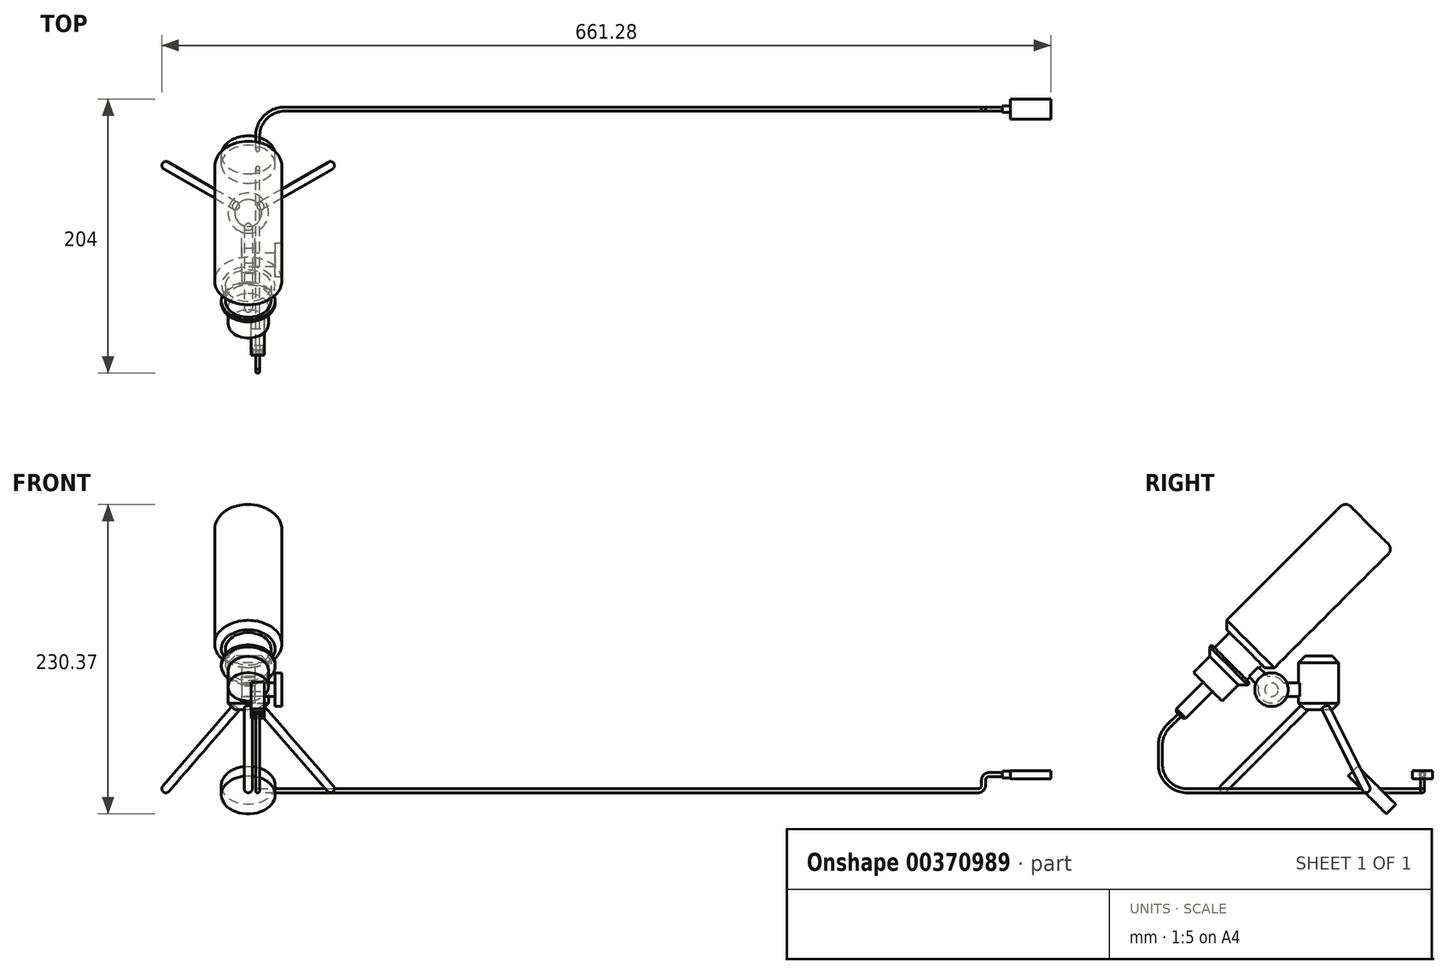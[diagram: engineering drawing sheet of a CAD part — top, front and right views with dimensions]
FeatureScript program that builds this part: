
annotation { "Feature Type Name" : "Feature", "Feature Type Description" : "" }
export const myFeature = defineFeature(function(context is Context, id is Id, definition is map)
    precondition{}
    {
        {
            var Q0;
            Q0=qCreatedBy(makeId("Top.planeOp"),FACE);
            var sketch = newSketch(context, id + "F0", { "sketchPlane" : qUnion([Q0])});
            skCircle(sketch, "E0", {"center": v(0, 0) * mm, "radius": 15 * mm});
            skSolve(sketch);
        }
        {
            var Q0;
            Q0=qSketchRegion(id+"F0",true);
            extrude(context, id + "F1", {"entities" : qUnion([Q0]), "depth" : 40 * mm});
        }
        {
            var Q0;
            Q0=makeQuery(id+"F1.opExtrude","CAP_EDGE",EDGE,{"disambiguationData":[OSD([sQuery(id+"F0.wireOp",EDGE,"E0")])],"isStart":true});
            var Q1;
            Q1=makeQuery(id+"F1.opExtrude","CAP_EDGE",EDGE,{"disambiguationData":[OSD([sQuery(id+"F0.wireOp",EDGE,"E0")])],"isStart":false});
            chamfer(context, id + "F2", {"entities" : qUnion([Q0, Q1]), "width" : 5 * mm, "tangentPropagation" : true});
        }
        {
            var Q0;
            Q0=qCreatedBy(makeId("Right.planeOp"),FACE);
            var sketch = newSketch(context, id + "F3", { "sketchPlane" : qUnion([Q0])});
            skLineSegment(sketch, "E1", {"start": v(-72.83, -56.59) * mm, "end": v(-2.12, 14.12) * mm});
            skLineSegment(sketch, "E2", {"start": v(-2.12, 14.12) * mm, "end": v(0, 12) * mm});
            skArc(sketch, "E3", {"start": v(-72.83, -56.59) * mm, "mid": v(-73.71, -58.71) * mm, "end": v(-72.83, -60.83) * mm});
            skLineSegment(sketch, "E4", {"start": v(-72.83, -60.83) * mm, "end": v(0, 12) * mm});
            skSolve(sketch);
        }
        {
            var Q0;
            Q0=qSketchRegion(id+"F3",true);
            var Q1;
            Q1=sQuery(id+"F3.wireOp",EDGE,"E4");
            revolve(context, id + "F4", {"operationType" : NewBodyOperationType.ADD, "entities" : qUnion([Q0]), "axis" : qUnion([Q1]), "revolveType" : RevolveType.FULL});
        }
        {
            var Q0;
            Q0=qCreatedBy(makeId("Right.planeOp"),FACE);
            var sketch = newSketch(context, id + "F5", { "sketchPlane" : qUnion([Q0])});
            skLineSegment(sketch, "E5", {"start": v(0, 0) * mm, "end": v(0, -28.47) * mm});
            skSolve(sketch);
        }
        {
            var Q0;
            Q0=qCreatedBy(makeId("Right.planeOp"),FACE);
            var Q1;
            Q1=sQuery(id+"F5.wireOp",EDGE,"E5");
            cPlane(context, id + "F6", {"entities" : qUnion([Q0, Q1]), "cplaneType" : CPlaneType.LINE_ANGLE, "offset" : 25 * mm, "angle" : 120 * degree, "oppositeDirection" : true, "width" : 150 * mm, "height" : 150 * mm});
        }
        {
            var Q0;
            Q0=qCreatedBy(id+"F6.planeOp",FACE);
            var sketch = newSketch(context, id + "F7", { "sketchPlane" : qUnion([Q0])});
            skLineSegment(sketch, "E6", {"start": v(0, 12) * mm, "end": v(72.73, -60.73) * mm});
            skLineSegment(sketch, "E7", {"start": v(72.73, -56.5) * mm, "end": v(2.02, 14.22) * mm});
            skLineSegment(sketch, "E8", {"start": v(2.02, 14.22) * mm, "end": v(0, 12) * mm});
            skArc(sketch, "E9", {"start": v(72.73, -56.5) * mm, "mid": v(73.61, -58.61) * mm, "end": v(72.73, -60.73) * mm});
            skPoint(sketch, "E10.orphan", {"position": v(70.61, -61.61) * mm});
            skSolve(sketch);
        }
        {
            var Q0;
            Q0=qSketchRegion(id+"F7",true);
            var Q1;
            Q1=sQuery(id+"F7.wireOp",EDGE,"E6");
            revolve(context, id + "F8", {"operationType" : NewBodyOperationType.ADD, "entities" : qUnion([Q0]), "axis" : qUnion([Q1]), "revolveType" : RevolveType.FULL});
        }
        {
            var Q0;
            Q0=qCreatedBy(id+"F6.planeOp",FACE);
            var Q1;
            Q1=sQuery(id+"F5.wireOp",EDGE,"E5");
            cPlane(context, id + "F9", {"entities" : qUnion([Q0, Q1]), "cplaneType" : CPlaneType.LINE_ANGLE, "offset" : 25 * mm, "angle" : 120 * degree, "oppositeDirection" : true, "width" : 150 * mm, "height" : 150 * mm});
        }
        {
            var Q0;
            Q0=qCreatedBy(id+"F9.planeOp",FACE);
            var sketch = newSketch(context, id + "F10", { "sketchPlane" : qUnion([Q0])});
            skLineSegment(sketch, "E11", {"start": v(0, 12) * mm, "end": v(-72.89, -60.89) * mm});
            skLineSegment(sketch, "E12", {"start": v(-72.89, -56.64) * mm, "end": v(-2.18, 14.07) * mm});
            skLineSegment(sketch, "E13", {"start": v(-2.18, 14.07) * mm, "end": v(0, 12) * mm});
            skArc(sketch, "E14", {"start": v(-72.89, -56.64) * mm, "mid": v(-73.77, -58.77) * mm, "end": v(-72.89, -60.89) * mm});
            skPoint(sketch, "E15.orphan", {"position": v(-70.77, -61.77) * mm});
            skSolve(sketch);
        }
        {
            var Q0;
            Q0=qSketchRegion(id+"F10",true);
            var Q1;
            Q1=sQuery(id+"F10.wireOp",EDGE,"E11");
            revolve(context, id + "F11", {"operationType" : NewBodyOperationType.ADD, "entities" : qUnion([Q0]), "axis" : qUnion([Q1]), "revolveType" : RevolveType.FULL});
        }
        {
            var Q0;
            Q0=qCreatedBy(makeId("Front.planeOp"),FACE);
            var sketch = newSketch(context, id + "F12", { "sketchPlane" : qUnion([Q0])});
            skLineSegment(sketch, "E16.bottom", {"start": v(-5, 20) * mm, "end": v(5, 20) * mm});
            skLineSegment(sketch, "E16.top", {"start": v(-5, 10) * mm, "end": v(5, 10) * mm});
            skLineSegment(sketch, "E16.left", {"start": v(-5, 20) * mm, "end": v(-5, 10) * mm});
            skLineSegment(sketch, "E16.right", {"start": v(5, 20) * mm, "end": v(5, 10) * mm});
            skSolve(sketch);
        }
        {
            var Q0;
            Q0=qSketchRegion(id+"F12",true);
            extrude(context, id + "F13", {"entities" : qUnion([Q0]), "operationType" : NewBodyOperationType.ADD, "depth" : 30 * mm});
        }
        {
            var Q0;
            Q0=qCreatedBy(makeId("Right.planeOp"),FACE);
            var sketch = newSketch(context, id + "F14", { "sketchPlane" : qUnion([Q0])});
            skCircle(sketch, "E17", {"center": v(-35, 15) * mm, "radius": 10 * mm});
            skLineSegment(sketch, "E18", {"start": v(-38.54, 11.46) * mm, "end": v(-35, 15) * mm});
            skLineSegment(sketch, "E19", {"start": v(-38.54, 11.46) * mm, "end": v(-52.68, 25.6) * mm});
            skLineSegment(sketch, "E20", {"start": v(-52.68, 25.6) * mm, "end": v(-45.6, 32.68) * mm});
            skLineSegment(sketch, "E21", {"start": v(-45.6, 32.68) * mm, "end": v(-31.46, 18.54) * mm});
            skLineSegment(sketch, "E22", {"start": v(-31.46, 18.54) * mm, "end": v(-35, 15) * mm});
            skSolve(sketch);
        }
        {
            var Q0;
            Q0=qSketchRegion(id+"F14",true);
            extrude(context, id + "F15", {"entities" : qUnion([Q0]), "operationType" : NewBodyOperationType.ADD, "endBound" : BoundingType.SYMMETRIC, "depth" : 10 * mm});
        }
        {
            var Q0;
            Q0=makeQuery(id+"F15.opExtrude","SWEPT_FACE",FACE,{"disambiguationData":[OSD([sQuery(id+"F14.wireOp",EDGE,"E21")])]});
            var sketch = newSketch(context, id + "F16", { "sketchPlane" : qUnion([Q0])});
            skPoint(sketch, "E23.first.point", {"position": v(0, -67.78) * mm});
            skPoint(sketch, "E23.first.point.positionSnap0", {"position": v(0, -55.36) * mm});
            skPoint(sketch, "E23.second.point", {"position": v(0, -49.63) * mm});
            skPoint(sketch, "E23.second.point.positionSnap0", {"position": v(0, -55.36) * mm});
            skPoint(sketch, "E23.third.point", {"position": v(-9.57, -55.36) * mm});
            skPoint(sketch, "E23.third.point.positionSnap0", {"position": v(0, -55.36) * mm});
            skCircle(sketch, "E24", {"center": v(0, -70.36) * mm, "radius": 20 * mm});
            skSolve(sketch);
        }
        {
            var Q0;
            Q0=qSketchRegion(id+"F16",true);
            extrude(context, id + "F17", {"entities" : qUnion([Q0]), "operationType" : NewBodyOperationType.ADD, "oppositeDirection" : true, "depth" : 10 * mm});
        }
        {
            var Q0;
            Q0=qCreatedBy(makeId("Right.planeOp"),FACE);
            var sketch = newSketch(context, id + "F18", { "sketchPlane" : qUnion([Q0])});
            skLineSegment(sketch, "E25", {"start": v(-82.38, 17.12) * mm, "end": v(37.83, 137.33) * mm});
            skLineSegment(sketch, "E26", {"start": v(37.83, 137.33) * mm, "end": v(20.15, 155) * mm});
            skLineSegment(sketch, "E27", {"start": v(20.15, 155) * mm, "end": v(-71.77, 63.08) * mm});
            skLineSegment(sketch, "E28", {"start": v(-71.77, 63.08) * mm, "end": v(-66.11, 57.43) * mm});
            skLineSegment(sketch, "E29", {"start": v(-66.11, 57.43) * mm, "end": v(-77.43, 46.11) * mm});
            skLineSegment(sketch, "E30", {"start": v(-84.5, 43.28) * mm, "end": v(-80.96, 39.75) * mm});
            skLineSegment(sketch, "E31", {"start": v(-89.45, 24.2) * mm, "end": v(-82.38, 17.12) * mm});
            skPoint(sketch, "E32.end.orphan", {"position": v(-71.77, 45.43) * mm});
            skLineSegment(sketch, "E33", {"start": v(-77.43, 46.11) * mm, "end": v(-79.55, 48.23) * mm});
            skLineSegment(sketch, "E34", {"start": v(-79.55, 48.23) * mm, "end": v(-84.5, 43.28) * mm});
            skLineSegment(sketch, "E35", {"start": v(-80.96, 39.75) * mm, "end": v(-92.98, 27.73) * mm});
            skLineSegment(sketch, "E36", {"start": v(-92.98, 27.73) * mm, "end": v(-89.45, 24.2) * mm});
            skPoint(sketch, "E37.start.orphan", {"position": v(-77.43, 36.21) * mm});
            skSolve(sketch);
        }
        {
            var Q0;
            Q0=qSketchRegion(id+"F18",true);
            var Q1;
            Q1=sQuery(id+"F18.wireOp",EDGE,"E25");
            revolve(context, id + "F19", {"operationType" : NewBodyOperationType.ADD, "entities" : qUnion([Q0]), "axis" : qUnion([Q1]), "revolveType" : RevolveType.FULL});
        }
        {
            var Q0;
            Q0=makeQuery(id+"F19.opRevolve","SWEPT_EDGE",EDGE,{"disambiguationData":[OSD([sQuery(id+"F18.wireOp",EDGE,"E26"),sQuery(id+"F18.wireOp",EDGE,"E27")])]});
            fillet(context, id + "F20", {"entities" : qUnion([Q0]), "radius" : 5 * mm, "tangentPropagation" : true, "allowEdgeOverflow" : false});
        }
        {
            var Q0;
            Q0=makeQuery(id+"F19.opRevolve","SWEPT_EDGE",EDGE,{"disambiguationData":[OSD([sQuery(id+"F18.wireOp",EDGE,"E27"),sQuery(id+"F18.wireOp",EDGE,"E28")])]});
            var Q1;
            Q1=makeQuery(id+"F19.opRevolve","SWEPT_EDGE",EDGE,{"disambiguationData":[OSD([sQuery(id+"F18.wireOp",EDGE,"E30"),sQuery(id+"F18.wireOp",EDGE,"E34")])]});
            chamfer(context, id + "F21", {"entities" : qUnion([Q0, Q1]), "width" : 5 * mm, "tangentPropagation" : true});
        }
        {
            var Q0;
            Q0=makeQuery(id+"F15.boolean.opBoolean","MERGE",FACE,{"derivedFrom":[makeQuery(id+"F13.opExtrude","SWEPT_FACE",FACE,{"disambiguationData":[OSD([sQuery(id+"F12.wireOp",EDGE,"E16.right")])]}),makeQuery(id+"F15.opExtrude","CAP_FACE",FACE,{"disambiguationData":[OSD([sQuery(id+"F14.wireOp",EDGE,"E17"),sQuery(id+"F14.wireOp",EDGE,"E19"),sQuery(id+"F14.wireOp",EDGE,"E20"),sQuery(id+"F14.wireOp",EDGE,"E21")])],"isStart":false})]});
            var sketch = newSketch(context, id + "F22", { "sketchPlane" : qUnion([Q0])});
            skCircle(sketch, "E38", {"center": v(-35, 15) * mm, "radius": 5 * mm});
            skSolve(sketch);
        }
        {
            var Q0;
            Q0=qSketchRegion(id+"F22",true);
            extrude(context, id + "F23", {"entities" : qUnion([Q0]), "operationType" : NewBodyOperationType.ADD, "depth" : 15 * mm});
        }
        {
            var Q0;
            Q0=makeQuery(id+"F23.opExtrude","CAP_FACE",FACE,{"disambiguationData":[OSD([sQuery(id+"F22.wireOp",EDGE,"E38")])],"isStart":false});
            var sketch = newSketch(context, id + "F24", { "sketchPlane" : qUnion([Q0])});
            skCircle(sketch, "E39", {"center": v(-35, 15) * mm, "radius": 12.5 * mm});
            skSolve(sketch);
        }
        {
            var Q0;
            Q0=qSketchRegion(id+"F24",true);
            extrude(context, id + "F25", {"entities" : qUnion([Q0]), "operationType" : NewBodyOperationType.ADD, "depth" : 5 * mm});
        }
        {
            var Q0;
            Q0=makeQuery(id+"F19.opRevolve","SWEPT_FACE",FACE,{"disambiguationData":[OSD([sQuery(id+"F18.wireOp",EDGE,"E31")])]});
            var sketch = newSketch(context, id + "F26", { "sketchPlane" : qUnion([Q0])});
            skLineSegment(sketch, "E40.bottom", {"start": v(2, 65.36) * mm, "end": v(12, 65.36) * mm});
            skLineSegment(sketch, "E40.top", {"start": v(2, 75.36) * mm, "end": v(12, 75.36) * mm});
            skLineSegment(sketch, "E40.left", {"start": v(2, 65.36) * mm, "end": v(2, 75.36) * mm});
            skLineSegment(sketch, "E40.right", {"start": v(12, 65.36) * mm, "end": v(12, 75.36) * mm});
            skSolve(sketch);
        }
        {
            var Q0;
            Q0=qSketchRegion(id+"F26",true);
            extrude(context, id + "F27", {"entities" : qUnion([Q0]), "operationType" : NewBodyOperationType.ADD, "depth" : 30 * mm});
        }
        {
            var Q0;
            Q0=makeQuery(id+"F27.opExtrude","CAP_FACE",FACE,{"disambiguationData":[OSD([sQuery(id+"F26.wireOp",EDGE,"E40.bottom"),sQuery(id+"F26.wireOp",EDGE,"E40.top"),sQuery(id+"F26.wireOp",EDGE,"E40.left"),sQuery(id+"F26.wireOp",EDGE,"E40.right")])],"isStart":false});
            chamfer(context, id + "F28", {"entities" : qUnion([Q0]), "width" : 2 * mm, "tangentPropagation" : true});
        }
        {
            var Q0;
            Q0=qCreatedBy(makeId("Right.planeOp"),FACE);
            var sketch = newSketch(context, id + "F29", { "sketchPlane" : qUnion([Q0])});
            skLineSegment(sketch, "E41", {"start": v(-103.59, -4.1) * mm, "end": v(-111.87, -12.38) * mm});
            skLineSegment(sketch, "E42", {"start": v(-117.73, -26.52) * mm, "end": v(-117.73, -40.23) * mm});
            skLineSegment(sketch, "E43", {"start": v(-97.73, -60.23) * mm, "end": v(52.27, -60.23) * mm});
            skPoint(sketch, "E44.visualSharp", {"position": v(-117.73, -18.23) * mm});
            skArc(sketch, "E44.filletArc", {"start": v(-111.87, -12.38) * mm, "mid": v(-116.2, -18.86) * mm, "end": v(-117.73, -26.52) * mm});
            skPoint(sketch, "E45.visualSharp", {"position": v(-117.73, -60.23) * mm});
            skArc(sketch, "E45.filletArc", {"start": v(-117.73, -40.23) * mm, "mid": v(-111.87, -54.38) * mm, "end": v(-97.73, -60.23) * mm});
            skSolve(sketch);
        }
        {
            var Q0;
            Q0=makeQuery(id+"F27.opExtrude","CAP_FACE",FACE,{"disambiguationData":[OSD([sQuery(id+"F26.wireOp",EDGE,"E40.bottom"),sQuery(id+"F26.wireOp",EDGE,"E40.top"),sQuery(id+"F26.wireOp",EDGE,"E40.left"),sQuery(id+"F26.wireOp",EDGE,"E40.right")])],"isStart":false});
            var sketch = newSketch(context, id + "F30", { "sketchPlane" : qUnion([Q0])});
            skCircle(sketch, "E46", {"center": v(7, 70.36) * mm, "radius": 1.5 * mm});
            skSolve(sketch);
        }
        {
            var Q0;
            Q0=qSketchRegion(id+"F30",true);
            var Q1;
            Q1=qConstructionFilter(qBodyType(qCreatedBy(id+"F29",EDGE),BodyType.WIRE),ConstructionObject.NO);
            sweep(context, id + "F31", {"operationType" : NewBodyOperationType.ADD, "profiles" : qUnion([Q0]), "path" : qUnion([Q1])});
        }
        {
            var Q0;
            Q0=makeQuery(id+"F31.opSweep","CAP_FACE",FACE,{"disambiguationData":[OSD([sQuery(id+"F29.wireOp",VERTEX,"E43.end"),sQuery(id+"F30.wireOp",EDGE,"E46")])],"isStart":false});
            var sketch = newSketch(context, id + "F32", { "sketchPlane" : qUnion([Q0])});
            skCircle(sketch, "E47", {"center": v(-7, -60.23) * mm, "radius": 1.5 * mm});
            skSolve(sketch);
        }
        {
            var Q0;
            Q0=qBodyType(qCreatedBy(id+"F32",EDGE),BodyType.WIRE);
            cPlane(context, id + "F33", {"entities" : qUnion([Q0]), "cplaneType" : CPlaneType.LINE_ANGLE, "offset" : 25 * mm, "angle" : 0 * degree, "width" : 150 * mm, "height" : 150 * mm});
        }
        {
            var Q0;
            Q0=qCreatedBy(id+"F33.planeOp",FACE);
            var sketch = newSketch(context, id + "F34", { "sketchPlane" : qUnion([Q0])});
            skLineSegment(sketch, "E48", {"start": v(27, 77.27) * mm, "end": v(527, 77.27) * mm});
            skLineSegment(sketch, "E49", {"start": v(7, 52.27) * mm, "end": v(7, 57.27) * mm});
            skArc(sketch, "E50", {"start": v(7, 57.27) * mm, "mid": v(12.86, 71.41) * mm, "end": v(27, 77.27) * mm});
            skSolve(sketch);
        }
        {
            var Q0;
            Q0=qSketchRegion(id+"F32",true);
            var Q1;
            Q1=qConstructionFilter(qBodyType(qCreatedBy(id+"F34",EDGE),BodyType.WIRE),ConstructionObject.NO);
            sweep(context, id + "F35", {"operationType" : NewBodyOperationType.ADD, "profiles" : qUnion([Q0]), "path" : qUnion([Q1])});
        }
        {
            var Q0;
            Q0=makeQuery(id+"F35.opSweep","CAP_FACE",FACE,{"disambiguationData":[OSD([sQuery(id+"F32.wireOp",EDGE,"E47"),sQuery(id+"F34.wireOp",VERTEX,"E48.end")])],"isStart":false});
            var sketch = newSketch(context, id + "F36", { "sketchPlane" : qUnion([Q0])});
            skCircle(sketch, "E51", {"center": v(77.27, -60.23) * mm, "radius": 1.5 * mm});
            skSolve(sketch);
        }
        {
            var Q0;
            Q0=sQuery(id+"F36.wireOp",EDGE,"E51");
            cPlane(context, id + "F37", {"entities" : qUnion([Q0]), "cplaneType" : CPlaneType.LINE_ANGLE, "offset" : 25 * mm, "angle" : 0 * degree, "width" : 150 * mm, "height" : 150 * mm});
        }
        {
            var Q0;
            Q0=qCreatedBy(id+"F37.planeOp",FACE);
            var sketch = newSketch(context, id + "F38", { "sketchPlane" : qUnion([Q0])});
            skLineSegment(sketch, "E52", {"start": v(-527, -60.23) * mm, "end": v(-543, -60.23) * mm});
            skLineSegment(sketch, "E53", {"start": v(-547, -56.23) * mm, "end": v(-547, -52.23) * mm});
            skLineSegment(sketch, "E54", {"start": v(-551, -48.23) * mm, "end": v(-567, -48.23) * mm});
            skArc(sketch, "E55", {"start": v(-543, -60.23) * mm, "mid": v(-545.83, -59.06) * mm, "end": v(-547, -56.23) * mm});
            skArc(sketch, "E56", {"start": v(-547, -52.23) * mm, "mid": v(-548.17, -49.4) * mm, "end": v(-551, -48.23) * mm});
            skPoint(sketch, "E57.0", {"position": v(-527, -60.23) * mm});
            skSolve(sketch);
        }
        {
            var Q0;
            Q0=qSketchRegion(id+"F36",true);
            var Q1;
            Q1=qConstructionFilter(qBodyType(qCreatedBy(id+"F38",EDGE),BodyType.WIRE),ConstructionObject.NO);
            sweep(context, id + "F39", {"operationType" : NewBodyOperationType.ADD, "profiles" : qUnion([Q0]), "path" : qUnion([Q1])});
        }
        {
            var Q0;
            Q0=makeQuery(id+"F39.opSweep","CAP_FACE",FACE,{"disambiguationData":[OSD([sQuery(id+"F36.wireOp",EDGE,"E51"),sQuery(id+"F38.wireOp",VERTEX,"E54.end")])],"isStart":false});
            var sketch = newSketch(context, id + "F40", { "sketchPlane" : qUnion([Q0])});
            skLineSegment(sketch, "E58.bottom", {"start": v(69.77, -51.23) * mm, "end": v(84.77, -51.23) * mm});
            skLineSegment(sketch, "E58.top", {"start": v(69.77, -45.23) * mm, "end": v(84.77, -45.23) * mm});
            skLineSegment(sketch, "E58.left", {"start": v(69.77, -51.23) * mm, "end": v(69.77, -45.23) * mm});
            skLineSegment(sketch, "E58.right", {"start": v(84.77, -51.23) * mm, "end": v(84.77, -45.23) * mm});
            skPoint(sketch, "E58.middle", {"position": v(77.27, -48.23) * mm});
            skSolve(sketch);
        }
        {
            var Q0;
            Q0=qSketchRegion(id+"F40",true);
            extrude(context, id + "F41", {"entities" : qUnion([Q0]), "operationType" : NewBodyOperationType.ADD, "depth" : 30 * mm});
        }
        {
            var Q0;
            Q0=makeQuery(id+"F41.opExtrude","CAP_FACE",FACE,{"disambiguationData":[OSD([sQuery(id+"F40.wireOp",EDGE,"E58.bottom"),sQuery(id+"F40.wireOp",EDGE,"E58.top"),sQuery(id+"F40.wireOp",EDGE,"E58.left"),sQuery(id+"F40.wireOp",EDGE,"E58.right")])],"isStart":true});
            var sketch = newSketch(context, id + "F42", { "sketchPlane" : qUnion([Q0])});
            skCircle(sketch, "E59", {"center": v(-77.27, -48.23) * mm, "radius": 2.5 * mm});
            skSolve(sketch);
        }
        {
            var Q0;
            Q0=qSketchRegion(id+"F42",true);
            extrude(context, id + "F43", {"entities" : qUnion([Q0]), "operationType" : NewBodyOperationType.ADD, "depth" : 6 * mm});
        }
    });
